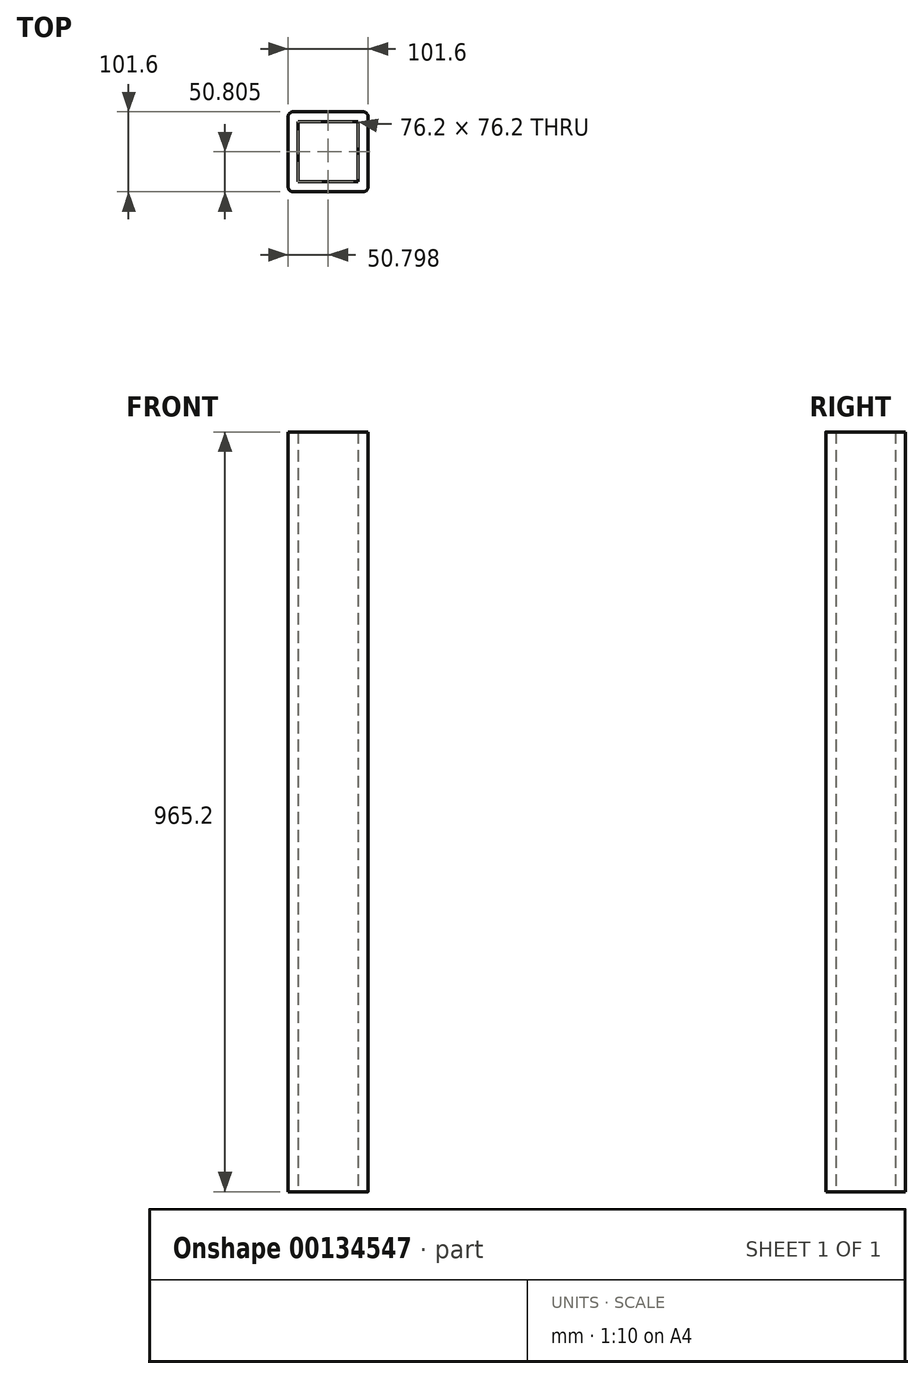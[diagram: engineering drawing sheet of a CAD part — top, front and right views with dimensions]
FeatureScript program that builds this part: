
annotation { "Feature Type Name" : "Feature", "Feature Type Description" : "" }
export const myFeature = defineFeature(function(context is Context, id is Id, definition is map)
    precondition{}
    {
        {
            var Q0;
            Q0=qCreatedBy(makeId("Top.planeOp"),FACE);
            var sketch = newSketch(context, id + "F0", { "sketchPlane" : qUnion([Q0])});
            skLineSegment(sketch, "E0", {"start": v(-31.86, 65.91) * mm, "end": v(-31.86, -22.99) * mm});
            skLineSegment(sketch, "E1", {"start": v(-25.51, -29.34) * mm, "end": v(63.39, -29.34) * mm});
            skLineSegment(sketch, "E2", {"start": v(69.74, -22.99) * mm, "end": v(69.74, 65.91) * mm});
            skLineSegment(sketch, "E3", {"start": v(63.39, 72.26) * mm, "end": v(-25.51, 72.26) * mm});
            skPoint(sketch, "E4.visualSharp", {"position": v(-31.86, 72.26) * mm});
            skArc(sketch, "E4.filletArc", {"start": v(-25.51, 72.26) * mm, "mid": v(-30, 70.4) * mm, "end": v(-31.86, 65.91) * mm});
            skPoint(sketch, "E5.visualSharp", {"position": v(69.74, 72.26) * mm});
            skArc(sketch, "E5.filletArc", {"start": v(69.74, 65.91) * mm, "mid": v(67.88, 70.4) * mm, "end": v(63.39, 72.26) * mm});
            skPoint(sketch, "E6.visualSharp", {"position": v(69.74, -29.34) * mm});
            skArc(sketch, "E6.filletArc", {"start": v(63.39, -29.34) * mm, "mid": v(67.88, -27.48) * mm, "end": v(69.74, -22.99) * mm});
            skPoint(sketch, "E7.visualSharp", {"position": v(-31.86, -29.34) * mm});
            skArc(sketch, "E7.filletArc", {"start": v(-31.86, -22.99) * mm, "mid": v(-30, -27.48) * mm, "end": v(-25.51, -29.34) * mm});
            skLineSegment(sketch, "E8.0", {"start": v(57.04, 59.56) * mm, "end": v(-19.16, 59.56) * mm});
            skLineSegment(sketch, "E8.1", {"start": v(57.04, -16.64) * mm, "end": v(57.04, 59.56) * mm});
            skLineSegment(sketch, "E8.2", {"start": v(-19.16, -16.64) * mm, "end": v(57.04, -16.64) * mm});
            skLineSegment(sketch, "E8.3", {"start": v(-19.16, 59.56) * mm, "end": v(-19.16, -16.64) * mm});
            skSolve(sketch);
        }
        {
            var Q0;
            Q0=makeQuery(id+"F0.imprint","IMPRINT",FACE,{"disambiguationData":[TD([[makeQuery(id+"F0.imprint","IMPRINT",EDGE,{"derivedFrom":sQuery(id+"F0.wireOp",EDGE,"E0")}),1.0]])]});
            extrude(context, id + "F1", {"entities" : qUnion([Q0]), "depth" : 965.2 * mm});
        }
    });
